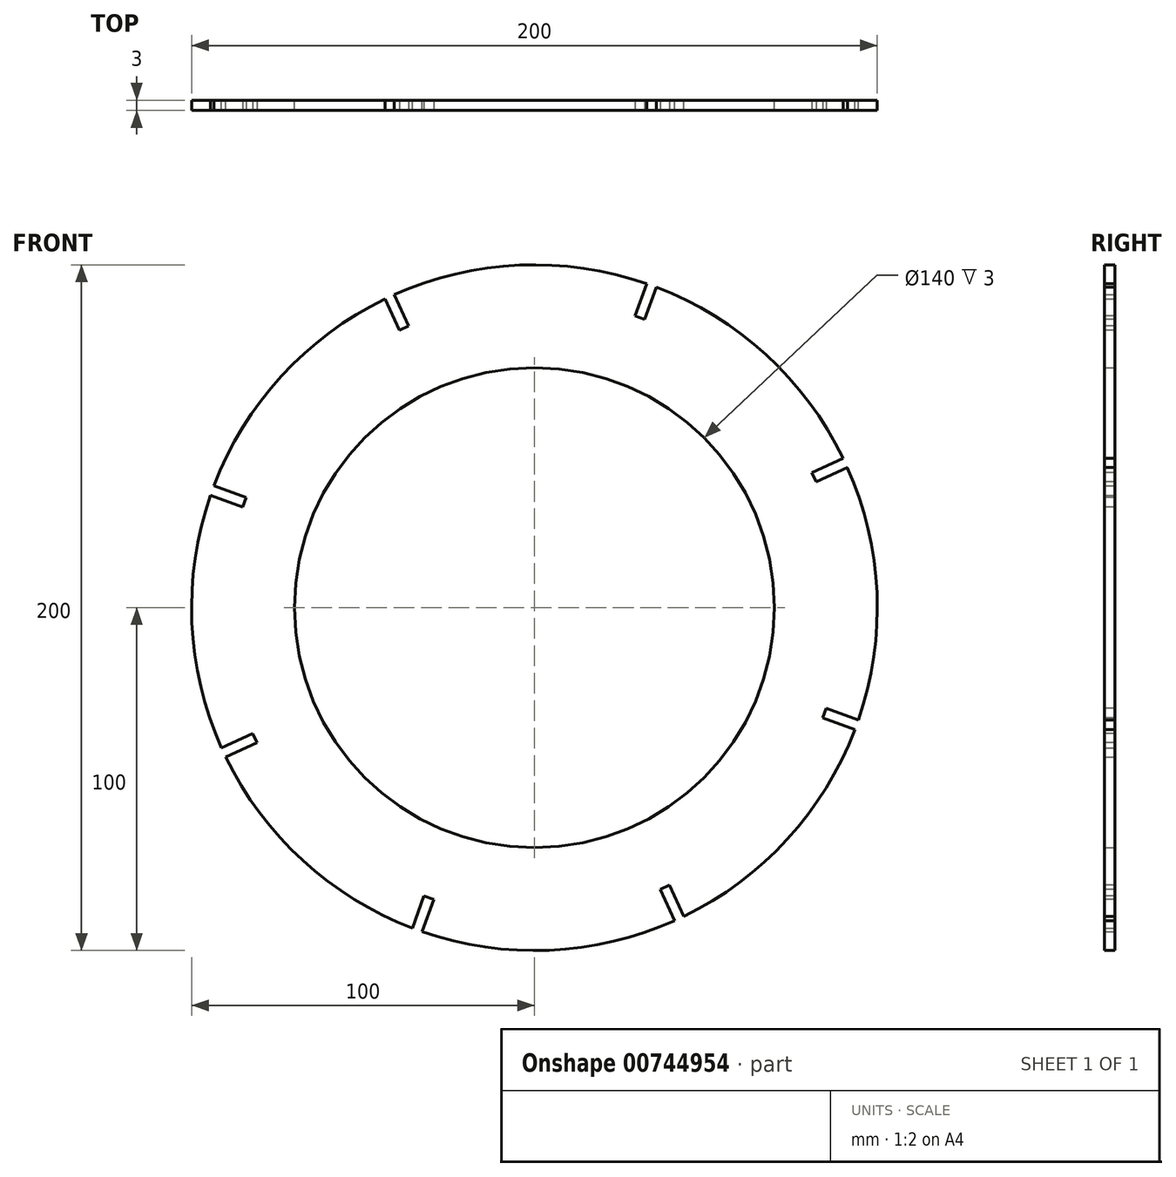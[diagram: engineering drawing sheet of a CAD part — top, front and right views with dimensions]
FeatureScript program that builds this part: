
annotation { "Feature Type Name" : "Feature", "Feature Type Description" : "" }
export const myFeature = defineFeature(function(context is Context, id is Id, definition is map)
    precondition{}
    {
        {
            var Q0;
            Q0=qCreatedBy(makeId("Front.planeOp"),FACE);
            var sketch = newSketch(context, id + "F0", { "sketchPlane" : qUnion([Q0])});
            skCircle(sketch, "E0", {"center": v(0, 0) * mm, "radius": 100 * mm});
            skCircle(sketch, "E1", {"center": v(0, 0) * mm, "radius": 70 * mm});
            skSolve(sketch);
        }
        {
            var Q0;
            Q0 = qSketchRegion(id + "F0", true);
            extrude(context, id + "F1", {"entities" : qUnion([Q0]), "depth" : 3 * mm, "offsetDistance" : 25 * mm});
        }
        {
            var Q0;
            Q0=makeQuery(id+"F1.opExtrude","CAP_FACE",FACE,{"disambiguationData":[OSD([sQuery(id+"F0.wireOp",EDGE,"E0"),sQuery(id+"F0.wireOp",EDGE,"E1")])],"isStart":false});
            var sketch = newSketch(context, id + "F2", { "sketchPlane" : qUnion([Q0])});
            skLineSegment(sketch, "E2", {"start": v(0, 0) * mm, "end": v(-103.94, 0) * mm, "construction": true});
            skLineSegment(sketch, "E3", {"start": v(0, 0) * mm, "end": v(-81.57, -38.04) * mm, "construction": true});
            skLineSegment(sketch, "E4.bottom", {"start": v(-100.33, -45.13) * mm, "end": v(-82.2, -36.68) * mm});
            skLineSegment(sketch, "E4.top", {"start": v(-99.06, -47.85) * mm, "end": v(-80.93, -39.4) * mm});
            skLineSegment(sketch, "E4.left", {"start": v(-100.33, -45.13) * mm, "end": v(-99.06, -47.85) * mm});
            skLineSegment(sketch, "E4.right", {"start": v(-82.2, -36.68) * mm, "end": v(-80.93, -39.4) * mm});
            skLineSegment(sketch, "E5.1.0", {"start": v(-36.21, -103.88) * mm, "end": v(-29.37, -85.09) * mm});
            skLineSegment(sketch, "E5.1.1", {"start": v(-39.03, -102.85) * mm, "end": v(-32.2, -84.06) * mm});
            skLineSegment(sketch, "E5.1.2", {"start": v(-32.2, -84.06) * mm, "end": v(-29.37, -85.09) * mm});
            skLineSegment(sketch, "E5.1.3", {"start": v(-39.03, -102.85) * mm, "end": v(-36.21, -103.88) * mm});
            skLineSegment(sketch, "E5.2.0", {"start": v(47.85, -99.06) * mm, "end": v(39.4, -80.93) * mm});
            skLineSegment(sketch, "E5.2.1", {"start": v(45.13, -100.33) * mm, "end": v(36.68, -82.2) * mm});
            skLineSegment(sketch, "E5.2.2", {"start": v(36.68, -82.2) * mm, "end": v(39.4, -80.93) * mm});
            skLineSegment(sketch, "E5.2.3", {"start": v(45.13, -100.33) * mm, "end": v(47.85, -99.06) * mm});
            skLineSegment(sketch, "E5.3.0", {"start": v(103.88, -36.21) * mm, "end": v(85.09, -29.37) * mm});
            skLineSegment(sketch, "E5.3.1", {"start": v(102.85, -39.03) * mm, "end": v(84.06, -32.2) * mm});
            skLineSegment(sketch, "E5.3.2", {"start": v(84.06, -32.2) * mm, "end": v(85.09, -29.37) * mm});
            skLineSegment(sketch, "E5.3.3", {"start": v(102.85, -39.03) * mm, "end": v(103.88, -36.21) * mm});
            skLineSegment(sketch, "E5.4.0", {"start": v(99.06, 47.85) * mm, "end": v(80.93, 39.4) * mm});
            skLineSegment(sketch, "E5.4.1", {"start": v(100.33, 45.13) * mm, "end": v(82.2, 36.68) * mm});
            skLineSegment(sketch, "E5.4.2", {"start": v(82.2, 36.68) * mm, "end": v(80.93, 39.4) * mm});
            skLineSegment(sketch, "E5.4.3", {"start": v(100.33, 45.13) * mm, "end": v(99.06, 47.85) * mm});
            skLineSegment(sketch, "E5.5.0", {"start": v(36.21, 103.88) * mm, "end": v(29.37, 85.09) * mm});
            skLineSegment(sketch, "E5.5.1", {"start": v(39.03, 102.85) * mm, "end": v(32.2, 84.06) * mm});
            skLineSegment(sketch, "E5.5.2", {"start": v(32.2, 84.06) * mm, "end": v(29.37, 85.09) * mm});
            skLineSegment(sketch, "E5.5.3", {"start": v(39.03, 102.85) * mm, "end": v(36.21, 103.88) * mm});
            skLineSegment(sketch, "E5.6.0", {"start": v(-47.85, 99.06) * mm, "end": v(-39.4, 80.93) * mm});
            skLineSegment(sketch, "E5.6.1", {"start": v(-45.13, 100.33) * mm, "end": v(-36.68, 82.2) * mm});
            skLineSegment(sketch, "E5.6.2", {"start": v(-36.68, 82.2) * mm, "end": v(-39.4, 80.93) * mm});
            skLineSegment(sketch, "E5.6.3", {"start": v(-45.13, 100.33) * mm, "end": v(-47.85, 99.06) * mm});
            skLineSegment(sketch, "E5.7.0", {"start": v(-103.88, 36.21) * mm, "end": v(-85.09, 29.37) * mm});
            skLineSegment(sketch, "E5.7.1", {"start": v(-102.85, 39.03) * mm, "end": v(-84.06, 32.2) * mm});
            skLineSegment(sketch, "E5.7.2", {"start": v(-84.06, 32.2) * mm, "end": v(-85.09, 29.37) * mm});
            skLineSegment(sketch, "E5.7.3", {"start": v(-102.85, 39.03) * mm, "end": v(-103.88, 36.21) * mm});
            skPoint(sketch, "E5.center", {"position": v(0, 0) * mm});
            skSolve(sketch);
        }
        {
            var Q0;
            Q0 = qSketchRegion(id + "F2", true);
            extrude(context, id + "F3", {"entities" : qUnion([Q0]), "operationType" : NewBodyOperationType.REMOVE, "oppositeDirection" : true, "depth" : 3 * mm, "offsetDistance" : 25 * mm});
        }
    });
